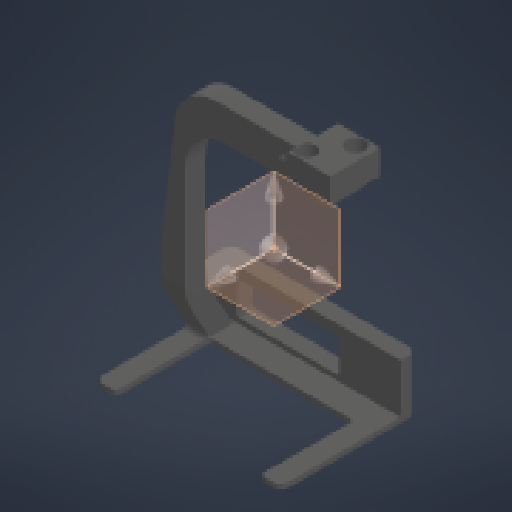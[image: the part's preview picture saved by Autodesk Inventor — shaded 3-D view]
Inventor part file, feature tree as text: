
AUTODESK INVENTOR PART (.ipt)
format: ipt  version: 2024.2 (Build 282272000, 272)  size: 606,720 bytes
history: native  units: in
note: dims shown in document units (in); Inventor stores cm internally (conversion verified against a paired STEP export)
features: reference x31, projected_geometry x23, extrude x21, sketch x14, other x11, fillet x10, chamfer x4, plane x1
ambient origin geometry x8: Origin, YZ Plane, XZ Plane, XY Plane, X Axis, Y Axis, Z Axis, Center Point
bodies: Solid1 (feature_tree)
feature tree (115):
  plane  "Work Plane1"
  extrude  "Extrusion1"  Depth=0.4in
  fillet  "Fillet1"  Radius=0.125in
  chamfer  "Chamfer1"  Distance=0.25in
  sketch  "Sketch3"  dims[d3=0.12in]
  extrude  "Extrusion2"  Depth=0.005in TaperAngle=45.0deg
  sketch  "Sketch4"  dims[d4=0.01in]
  extrude  "Extrusion5"  Depth=1.69in
  sketch  "Sketch5"  dims[d5=0.0625in d6=0.25in d7=0.0in]
  extrude  "Extrusion6"  Depth=2.263in
  extrude  "Extrusion7"  Depth=0.25in
  extrude  "Extrusion8"  Depth=0.5841in
  extrude  "Extrusion9"  Depth=0.3in TaperAngle=0.0deg
  sketch  "Sketch7"  dims[d12=0.0625in d13=0.0in d16=1.69in]
  extrude  "Extrusion10"  Depth=0.5in
  extrude  "Extrusion11"  Depth=0.05in
  fillet  "Fillet6"  [1 undecoded]
  fillet  "Fillet7"  Radius=0.25in
  fillet  "Fillet8"  Radius=0.2865in
  extrude  "Extrusion12"  Depth=0.25in TaperAngle=0.0deg
  extrude  "Extrusion13"  Depth=0.05in
  extrude  "Extrusion14"  TaperAngle=0.0deg  [1 undecoded]
  extrude  "Extrusion15"  Depth=0.05in
  extrude  "Extrusion17"  TaperAngle=0.0deg  [1 undecoded]
  extrude  "Extrusion18"  Depth=0.05in TaperAngle=0.0deg
  extrude  "Extrusion19"  Depth=0.05in
  fillet  "Fillet10"  Radius=0.3313in
  sketch  "Sketch17"  dims[d40=0.5in d41=0.1in d42=0.0in d43=0.0in d44=0.05in d45=0.0in d46=0.0in d47=0.3361in d48=0.0in d49=0.1236in d50=0.3313in d51=0.385in d52=0.6in d53=0.0in d54=0.7in d55=0.0in d56=1.0in d57=0.0in d59=0.125in d60=0.125in d61=0.0in d62=0.125in d63=0.125in d64=45.0deg d67=0.16in d68=0.45in d69=0.0in d70=0.0in d71=2.0in d72=0.0in d73=0.5in d74=0.0in d75=0.05in d76=0.222in d78=0.222in d82=0.015in d83=0.431in d84=0.431in d87=0.1in d88=0.125in d89=45.0deg d90=0.5in d91=0.0in d92=0.15in d93=0.0in d94=0.0in d95=0.0in d96=0.05in d97=0.125in d98=0.125in d99=45.0deg d100=0.075in d101=0.05in d77=0.5in]
  extrude  "Extrusion21"  Depth=0.05in
  extrude  "Extrusion22"  Depth=0.05in TaperAngle=0.0deg
  extrude  "Extrusion23"  Depth=0.05in TaperAngle=0.0deg
  fillet  "Fillet11"  Radius=1.0in
  chamfer  "Chamfer4"  Distance=0.125in
  fillet  "Fillet12"  Radius=0.125in
  fillet  "Fillet13"  Radius=0.125in
  chamfer  "Chamfer3"  Distance=0.16in
  chamfer  "Chamfer2"  Distance=2.0in
  extrude  "Extrusion3"  Depth=0.05in TaperAngle=0.0deg
  extrude  "Extrusion4"  Depth=0.05in
  fillet  "Fillet4"  Radius=0.222in
  fillet  "Fillet5"  Radius=0.222in
  sketch  "Sketch2"  dims[d0=0.005in d1=0.4in d2=0.125in]
  reference  "Reference2"
  reference  "Reference3"
  reference  "Reference4"
  reference  "Reference5"
  reference  "Reference6"
  reference  "Reference7"
  reference  "Reference8"
  reference  "Reference9"
  reference  "Reference10"
  reference  "Reference11"
  reference  "Reference12"
  reference  "Reference13"
  reference  "Reference14"
  reference  "Reference15"
  reference  "Reference16"
  reference  "Reference17"
  reference  "Reference18"
  reference  "Reference19"
  reference  "Reference20"
  reference  "Reference21"
  reference  "Reference22"
  reference  "Reference23"
  reference  "Reference24"
  reference  "Reference25"
  reference  "Reference26"
  projected_geometry  "Projected Loop1"
  reference  "Reference27"
  reference  "Reference28"
  reference  "Reference29"
  reference  "Reference30"
  reference  "Reference31"
  projected_geometry  "Projected Loop2"
  projected_geometry  "Projected Loop3"
  projected_geometry  "Projected Loop4"
  sketch  "Sketch6"  dims[d8=0.5in d9=0.005in d10=0.125in d11=45.0deg]
  projected_geometry  "Projected Loop5"
  projected_geometry  "Projected Loop6"
  projected_geometry  "Projected Loop7"
  projected_geometry  "Projected Loop8"
  sketch  "Sketch8"  dims[d17=2.263in d18=2.263in]
  projected_geometry  "Projected Loop9"
  reference  "Reference32"
  projected_geometry  "Projected Loop10"
  projected_geometry  "Projected Loop11"
  sketch  "Sketch9"  dims[d19=0.25in d20=0.25in]
  projected_geometry  "Projected Loop12"
  sketch  "Sketch10"  dims[d21=0.6528in d22=0.5841in]
  projected_geometry  "Projected Loop13"
  projected_geometry  "Projected Loop14"
  projected_geometry  "Projected Loop15"
  projected_geometry  "Projected Loop16"
  sketch  "Sketch11"  dims[d23=0.25in d24=0.0in d25=0.3in d26=0.0in]
  projected_geometry  "Projected Loop19"
  sketch  "Sketch14"  dims[d27=0.125in d28=0.0in d29=0.5in]
  projected_geometry  "Projected Loop20"
  sketch  "Sketch15"  dims[d30=0.125in d31=0.05in d32=120.0deg d33=0.25in d34=0.2865in d35=0.0in]
  projected_geometry  "Projected Loop21"
  sketch  "Sketch16"  dims[d36=0.0in d37=0.0in d38=0.25in d39=0.0in]
  projected_geometry  "Projected Loop22"
  projected_geometry  "Projected Loop23"
  projected_geometry  "Projected Loop24"
  projected_geometry  "Projected Loop25"
  other  "<userpath>\Documents\School\FallCAD\Bio\Bio.iam"
  other  "Bio.iam"
  other  "Servo HS425BB:1"
  other  "ServoMount:1"
  other  "92095A186_Button Head Hex Drive Screw:1"
  other  "92095A186_Button Head Hex Drive Screw:2"
  other  "90576A102_Medium-Strength Steel Nylon-Insert Locknut:4"
  other  "FrontLinkage:1"
  other  "90576A102_Medium-Strength Steel Nylon-Insert Locknut:2"
  other  "90576A102_Medium-Strength Steel Nylon-Insert Locknut:1"
  other  "Leg_MIR:1"
note: 3 required parameter values undecoded (feature->parameter linkage not recoverable at this tier; creation-order binding heuristic only, values carry confidence <= 0.55)
